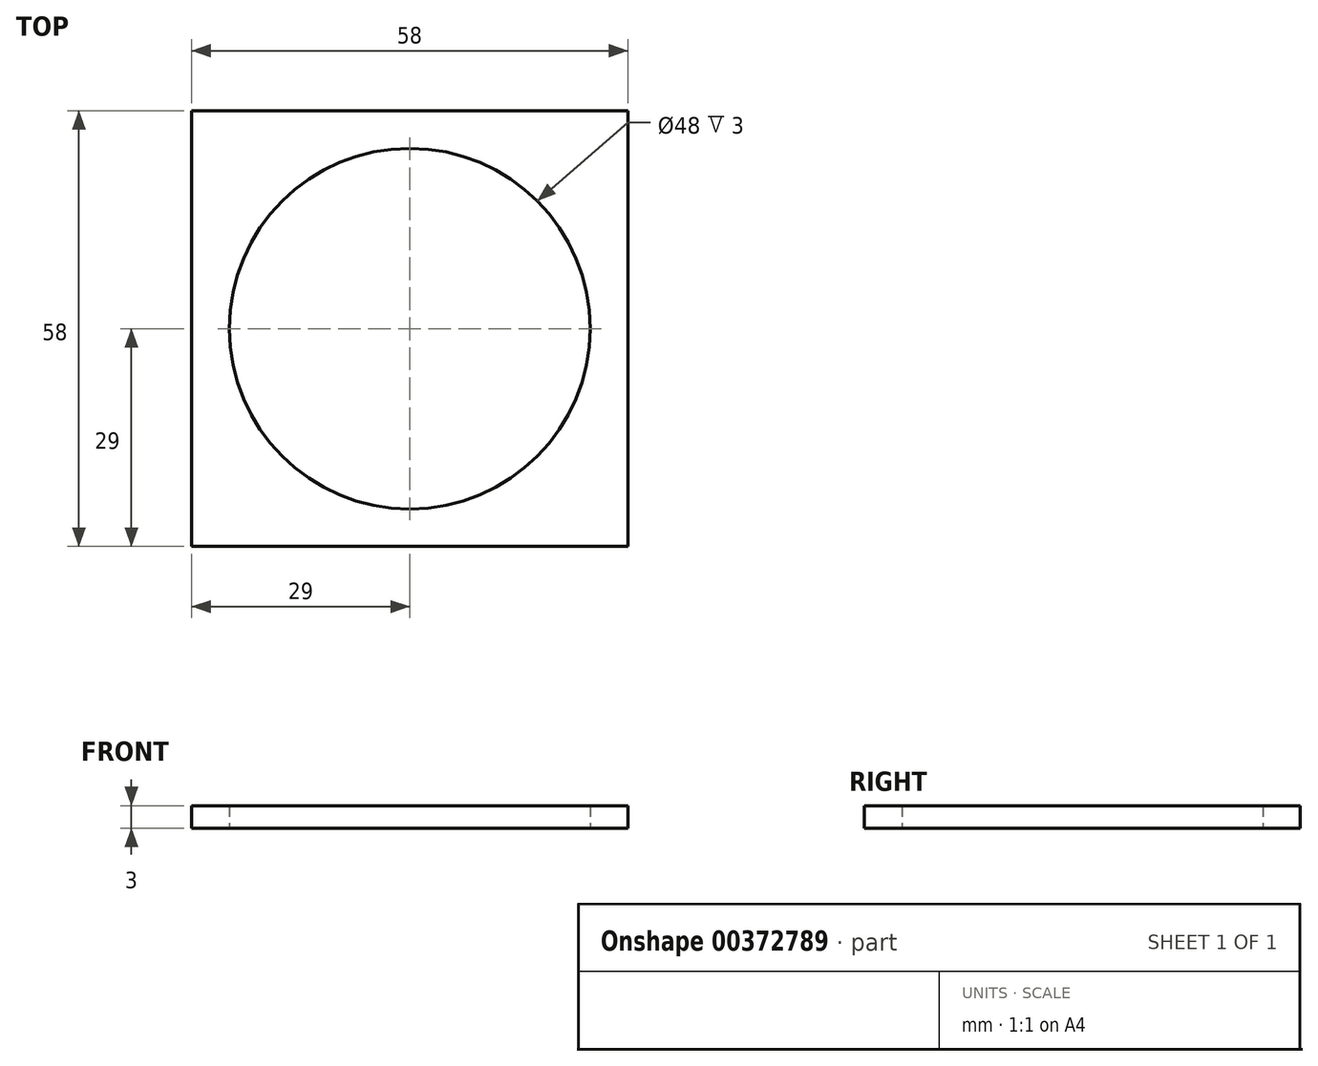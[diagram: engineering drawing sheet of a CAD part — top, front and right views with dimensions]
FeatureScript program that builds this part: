
annotation { "Feature Type Name" : "Feature", "Feature Type Description" : "" }
export const myFeature = defineFeature(function(context is Context, id is Id, definition is map)
    precondition{}
    {
        {
            var Q0;
            Q0=qCreatedBy(makeId("Top.planeOp"),FACE);
            var sketch = newSketch(context, id + "F0", { "sketchPlane" : qUnion([Q0])});
            skLineSegment(sketch, "E0.bottom", {"start": v(29, -29) * mm, "end": v(-29, -29) * mm});
            skLineSegment(sketch, "E0.top", {"start": v(29, 29) * mm, "end": v(-29, 29) * mm});
            skLineSegment(sketch, "E0.left", {"start": v(29, -29) * mm, "end": v(29, 29) * mm});
            skLineSegment(sketch, "E0.right", {"start": v(-29, -29) * mm, "end": v(-29, 29) * mm});
            skPoint(sketch, "E0.middle", {"position": v(0, 0) * mm});
            skCircle(sketch, "E1", {"center": v(0, 0) * mm, "radius": 24 * mm});
            skSolve(sketch);
        }
        {
            var Q0;
            Q0=makeQuery(id+"F0.imprint","IMPRINT",FACE,{"disambiguationData":[TD([[makeQuery(id+"F0.imprint","IMPRINT",EDGE,{"derivedFrom":sQuery(id+"F0.wireOp",EDGE,"E0.bottom")}),-1.0]])]});
            extrude(context, id + "F1", {"entities" : qUnion([Q0]), "depth" : 3 * mm});
        }
    });
